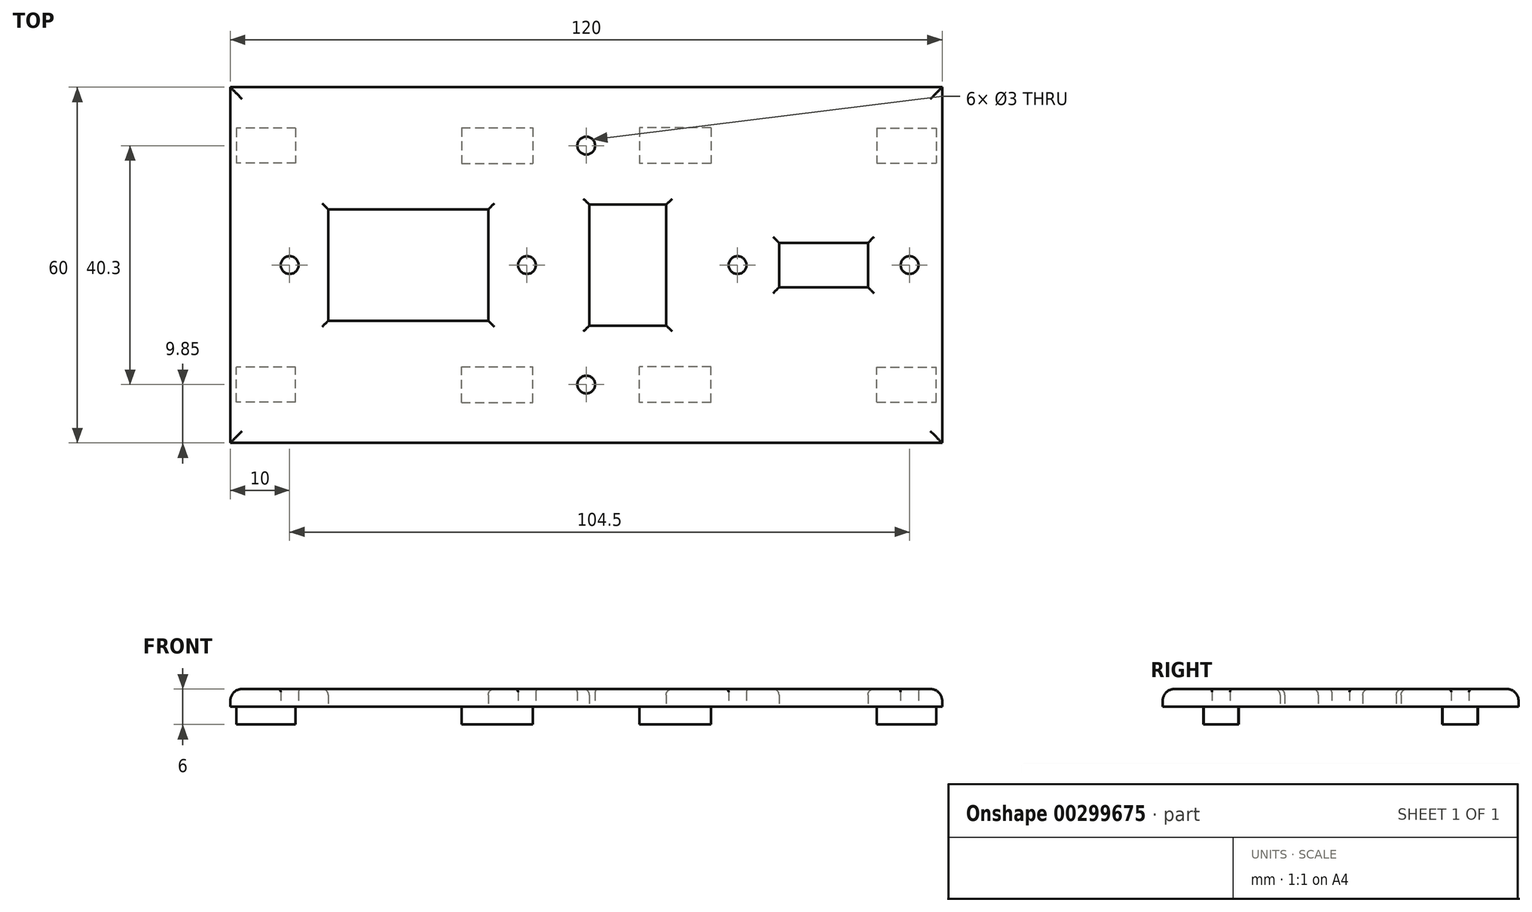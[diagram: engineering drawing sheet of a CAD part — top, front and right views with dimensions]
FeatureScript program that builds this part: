
annotation { "Feature Type Name" : "Feature", "Feature Type Description" : "" }
export const myFeature = defineFeature(function(context is Context, id is Id, definition is map)
    precondition{}
    {
        {
            var Q0;
            Q0=qCreatedBy(makeId("Top.planeOp"),FACE);
            var sketch = newSketch(context, id + "F0", { "sketchPlane" : qUnion([Q0])});
            skLineSegment(sketch, "E0.bottom", {"start": v(60, 30) * mm, "end": v(-60, 30) * mm});
            skLineSegment(sketch, "E0.top", {"start": v(60, -30) * mm, "end": v(-60, -30) * mm});
            skLineSegment(sketch, "E0.left", {"start": v(60, 30) * mm, "end": v(60, -30) * mm});
            skLineSegment(sketch, "E0.right", {"start": v(-60, 30) * mm, "end": v(-60, -30) * mm});
            skPoint(sketch, "E0.middle", {"position": v(0, 0) * mm});
            skLineSegment(sketch, "E1", {"start": v(0, 0) * mm, "end": v(0, 20.15) * mm, "construction": true});
            skLineSegment(sketch, "E2", {"start": v(-60, 20.15) * mm, "end": v(60, 20.15) * mm, "construction": true});
            skLineSegment(sketch, "E3", {"start": v(-60, 20.15) * mm, "end": v(-53.98, 20.15) * mm, "construction": true});
            skLineSegment(sketch, "E4.bottom", {"start": v(-48.98, 23.1) * mm, "end": v(-58.98, 23.1) * mm});
            skLineSegment(sketch, "E4.top", {"start": v(-48.98, 17.2) * mm, "end": v(-58.98, 17.2) * mm});
            skLineSegment(sketch, "E4.left", {"start": v(-48.98, 23.1) * mm, "end": v(-48.98, 17.2) * mm});
            skLineSegment(sketch, "E4.right", {"start": v(-58.98, 23.1) * mm, "end": v(-58.98, 17.2) * mm});
            skPoint(sketch, "E4.middle", {"position": v(-53.98, 20.15) * mm});
            skLineSegment(sketch, "E5", {"start": v(0, 20.15) * mm, "end": v(-15, 20.15) * mm, "construction": true});
            skLineSegment(sketch, "E6.bottom", {"start": v(-21.02, 23.15) * mm, "end": v(-8.98, 23.15) * mm});
            skLineSegment(sketch, "E6.top", {"start": v(-21.02, 17.15) * mm, "end": v(-8.98, 17.15) * mm});
            skLineSegment(sketch, "E6.left", {"start": v(-21.02, 23.15) * mm, "end": v(-21.02, 17.15) * mm});
            skLineSegment(sketch, "E6.right", {"start": v(-8.98, 23.15) * mm, "end": v(-8.98, 17.15) * mm});
            skPoint(sketch, "E6.middle", {"position": v(-15, 20.15) * mm});
            skLineSegment(sketch, "E7.MirrorCS", {"start": v(48.98, 23.1) * mm, "end": v(58.98, 23.1) * mm});
            skLineSegment(sketch, "E8.MirrorCS", {"start": v(48.98, 17.2) * mm, "end": v(58.98, 17.2) * mm});
            skLineSegment(sketch, "E9.MirrorCS", {"start": v(58.98, 23.1) * mm, "end": v(58.98, 17.2) * mm});
            skLineSegment(sketch, "E10.MirrorCS", {"start": v(48.98, 23.1) * mm, "end": v(48.98, 17.2) * mm});
            skLineSegment(sketch, "E11.MirrorCS", {"start": v(21.02, 17.15) * mm, "end": v(8.98, 17.15) * mm});
            skLineSegment(sketch, "E12.MirrorCS", {"start": v(21.02, 23.15) * mm, "end": v(8.98, 23.15) * mm});
            skLineSegment(sketch, "E13.MirrorCS", {"start": v(21.02, 23.15) * mm, "end": v(21.02, 17.15) * mm});
            skLineSegment(sketch, "E14.MirrorCS", {"start": v(8.98, 23.15) * mm, "end": v(8.98, 17.15) * mm});
            skLineSegment(sketch, "E15.MirrorCS", {"start": v(-58.98, -23.1) * mm, "end": v(-58.98, -17.2) * mm});
            skLineSegment(sketch, "E16.MirrorCS", {"start": v(-48.98, -23.1) * mm, "end": v(-48.98, -17.2) * mm});
            skLineSegment(sketch, "E17.MirrorCS", {"start": v(-21.02, -23.15) * mm, "end": v(-21.02, -17.15) * mm});
            skLineSegment(sketch, "E18.MirrorCS", {"start": v(-8.98, -23.15) * mm, "end": v(-8.98, -17.15) * mm});
            skLineSegment(sketch, "E19.MirrorCS", {"start": v(8.98, -23.15) * mm, "end": v(8.98, -17.15) * mm});
            skLineSegment(sketch, "E20.MirrorCS", {"start": v(21.02, -23.15) * mm, "end": v(21.02, -17.15) * mm});
            skLineSegment(sketch, "E21.MirrorCS", {"start": v(48.98, -23.1) * mm, "end": v(48.98, -17.2) * mm});
            skLineSegment(sketch, "E22.MirrorCS", {"start": v(58.98, -23.1) * mm, "end": v(58.98, -17.2) * mm});
            skLineSegment(sketch, "E23.MirrorCS", {"start": v(48.98, -23.1) * mm, "end": v(58.98, -23.1) * mm});
            skLineSegment(sketch, "E24.MirrorCS", {"start": v(21.02, -23.15) * mm, "end": v(8.98, -23.15) * mm});
            skLineSegment(sketch, "E25.MirrorCS", {"start": v(-21.02, -23.15) * mm, "end": v(-8.98, -23.15) * mm});
            skLineSegment(sketch, "E26.MirrorCS", {"start": v(-48.98, -23.1) * mm, "end": v(-58.98, -23.1) * mm});
            skLineSegment(sketch, "E27.MirrorCS", {"start": v(-48.98, -17.2) * mm, "end": v(-58.98, -17.2) * mm});
            skLineSegment(sketch, "E28.MirrorCS", {"start": v(-21.02, -17.15) * mm, "end": v(-8.98, -17.15) * mm});
            skLineSegment(sketch, "E29.MirrorCS", {"start": v(21.02, -17.15) * mm, "end": v(8.98, -17.15) * mm});
            skLineSegment(sketch, "E30.MirrorCS", {"start": v(48.98, -17.2) * mm, "end": v(58.98, -17.2) * mm});
            skLineSegment(sketch, "E31", {"start": v(0, 0) * mm, "end": v(-30, 0) * mm, "construction": true});
            skLineSegment(sketch, "E32.bottom", {"start": v(-43.5, -9.4) * mm, "end": v(-16.5, -9.4) * mm});
            skLineSegment(sketch, "E32.top", {"start": v(-43.5, 9.4) * mm, "end": v(-16.5, 9.4) * mm});
            skLineSegment(sketch, "E32.left", {"start": v(-43.5, -9.4) * mm, "end": v(-43.5, 9.4) * mm});
            skLineSegment(sketch, "E32.right", {"start": v(-16.5, -9.4) * mm, "end": v(-16.5, 9.4) * mm});
            skPoint(sketch, "E32.middle", {"position": v(-30, 0) * mm});
            skLineSegment(sketch, "E33", {"start": v(60, 0) * mm, "end": v(40, 0) * mm, "construction": true});
            skPoint(sketch, "E33.endSnap0", {"position": v(60, 0) * mm});
            skLineSegment(sketch, "E34.bottom", {"start": v(47.5, 3.75) * mm, "end": v(32.5, 3.75) * mm});
            skLineSegment(sketch, "E34.top", {"start": v(47.5, -3.75) * mm, "end": v(32.5, -3.75) * mm});
            skLineSegment(sketch, "E34.left", {"start": v(47.5, 3.75) * mm, "end": v(47.5, -3.75) * mm});
            skLineSegment(sketch, "E34.right", {"start": v(32.5, 3.75) * mm, "end": v(32.5, -3.75) * mm});
            skPoint(sketch, "E34.middle", {"position": v(40, 0) * mm});
            skLineSegment(sketch, "E35", {"start": v(-30, 0) * mm, "end": v(-50, 0) * mm, "construction": true});
            skLineSegment(sketch, "E36", {"start": v(-30, 0) * mm, "end": v(-10, 0) * mm, "construction": true});
            skCircle(sketch, "E37", {"center": v(-10, 0) * mm, "radius": 1.5 * mm});
            skLineSegment(sketch, "E38", {"start": v(-30, 0) * mm, "end": v(-30, 7) * mm, "construction": true});
            skCircle(sketch, "E39.MirrorC", {"center": v(-50, 0) * mm, "radius": 1.5 * mm});
            skLineSegment(sketch, "E40", {"start": v(40, 0) * mm, "end": v(25.5, 0) * mm, "construction": true});
            skLineSegment(sketch, "E41", {"start": v(40, 0) * mm, "end": v(40, 7) * mm, "construction": true});
            skPoint(sketch, "E41.endSnap0", {"position": v(40, 3.75) * mm});
            skCircle(sketch, "E42", {"center": v(25.5, 0) * mm, "radius": 1.5 * mm});
            skCircle(sketch, "E43.MirrorC", {"center": v(54.5, 0) * mm, "radius": 1.5 * mm});
            skCircle(sketch, "E44", {"center": v(0, 20.15) * mm, "radius": 1.5 * mm});
            skCircle(sketch, "E45.MirrorC", {"center": v(0, -20.15) * mm, "radius": 1.5 * mm});
            skLineSegment(sketch, "E46", {"start": v(0, 0) * mm, "end": v(7, 0) * mm, "construction": true});
            skLineSegment(sketch, "E47.bottom", {"start": v(13.47, 10.2) * mm, "end": v(0.52, 10.2) * mm});
            skLineSegment(sketch, "E47.top", {"start": v(13.48, -10.2) * mm, "end": v(0.53, -10.2) * mm});
            skLineSegment(sketch, "E47.left", {"start": v(13.47, 10.2) * mm, "end": v(13.48, -10.2) * mm});
            skLineSegment(sketch, "E47.right", {"start": v(0.52, 10.2) * mm, "end": v(0.53, -10.2) * mm});
            skPoint(sketch, "E47.middle", {"position": v(7, 0) * mm});
            skSolve(sketch);
        }
        {
            var Q0;
            Q0 = qSketchRegion(id + "F0", true);
            var Q1;
            Q1=makeQuery(id+"F0.imprint","IMPRINT",FACE,{"disambiguationData":[TD([[makeQuery(id+"F0.imprint","IMPRINT",EDGE,{"derivedFrom":sQuery(id+"F0.wireOp",EDGE,"E6.bottom")}),-1.0]])]});
            var Q2;
            Q2=makeQuery(id+"F0.imprint","IMPRINT",FACE,{"disambiguationData":[TD([[makeQuery(id+"F0.imprint","IMPRINT",EDGE,{"derivedFrom":sQuery(id+"F0.wireOp",EDGE,"E11.MirrorCS")}),-1.0]])]});
            var Q3;
            Q3=makeQuery(id+"F0.imprint","IMPRINT",FACE,{"disambiguationData":[TD([[makeQuery(id+"F0.imprint","IMPRINT",EDGE,{"derivedFrom":sQuery(id+"F0.wireOp",EDGE,"E19.MirrorCS")}),-1.0]])]});
            var Q4;
            Q4=makeQuery(id+"F0.imprint","IMPRINT",FACE,{"disambiguationData":[TD([[makeQuery(id+"F0.imprint","IMPRINT",EDGE,{"derivedFrom":sQuery(id+"F0.wireOp",EDGE,"E17.MirrorCS")}),-1.0]])]});
            var Q5;
            Q5=makeQuery(id+"F0.imprint","IMPRINT",FACE,{"disambiguationData":[TD([[makeQuery(id+"F0.imprint","IMPRINT",EDGE,{"derivedFrom":sQuery(id+"F0.wireOp",EDGE,"E4.bottom")}),1.0]])]});
            var Q6;
            Q6=makeQuery(id+"F0.imprint","IMPRINT",FACE,{"disambiguationData":[TD([[makeQuery(id+"F0.imprint","IMPRINT",EDGE,{"derivedFrom":sQuery(id+"F0.wireOp",EDGE,"E15.MirrorCS")}),-1.0]])]});
            var Q7;
            Q7=makeQuery(id+"F0.imprint","IMPRINT",FACE,{"disambiguationData":[TD([[makeQuery(id+"F0.imprint","IMPRINT",EDGE,{"derivedFrom":sQuery(id+"F0.wireOp",EDGE,"E21.MirrorCS")}),-1.0]])]});
            var Q8;
            Q8=makeQuery(id+"F0.imprint","IMPRINT",FACE,{"disambiguationData":[TD([[makeQuery(id+"F0.imprint","IMPRINT",EDGE,{"derivedFrom":sQuery(id+"F0.wireOp",EDGE,"E7.MirrorCS")}),-1.0]])]});
            extrude(context, id + "F1", {"entities" : qUnion([Q0, Q1, Q2, Q3, Q4, Q5, Q6, Q7, Q8]), "depth" : 3 * mm});
        }
        {
            var Q0;
            Q0=makeQuery(id+"F1.opExtrude","CAP_EDGE",EDGE,{"disambiguationData":[OSD([sQuery(id+"F0.wireOp",EDGE,"E0.top")])],"isStart":false});
            var Q1;
            Q1=makeQuery(id+"F1.opExtrude","CAP_EDGE",EDGE,{"disambiguationData":[OSD([sQuery(id+"F0.wireOp",EDGE,"E0.bottom")])],"isStart":false});
            var Q2;
            Q2=makeQuery(id+"F1.opExtrude","CAP_EDGE",EDGE,{"disambiguationData":[OSD([sQuery(id+"F0.wireOp",EDGE,"E0.right")])],"isStart":false});
            var Q3;
            Q3=makeQuery(id+"F1.opExtrude","CAP_EDGE",EDGE,{"disambiguationData":[OSD([sQuery(id+"F0.wireOp",EDGE,"E0.left")])],"isStart":false});
            fillet(context, id + "F2", {"entities" : qUnion([Q0, Q1, Q2, Q3]), "radius" : 2 * mm, "tangentPropagation" : true, "allowEdgeOverflow" : false});
        }
        {
            var Q0;
            Q0=makeQuery(id+"F1.opExtrude","CAP_EDGE",EDGE,{"disambiguationData":[OSD([sQuery(id+"F0.wireOp",EDGE,"E34.left")])],"isStart":false});
            var Q1;
            Q1=makeQuery(id+"F1.opExtrude","CAP_EDGE",EDGE,{"disambiguationData":[OSD([sQuery(id+"F0.wireOp",EDGE,"E34.right")])],"isStart":false});
            var Q2;
            Q2=makeQuery(id+"F1.opExtrude","CAP_EDGE",EDGE,{"disambiguationData":[OSD([sQuery(id+"F0.wireOp",EDGE,"E34.bottom")])],"isStart":false});
            var Q3;
            Q3=makeQuery(id+"F1.opExtrude","CAP_EDGE",EDGE,{"disambiguationData":[OSD([sQuery(id+"F0.wireOp",EDGE,"E34.top")])],"isStart":false});
            var Q4;
            Q4=makeQuery(id+"F1.opExtrude","CAP_EDGE",EDGE,{"disambiguationData":[OSD([sQuery(id+"F0.wireOp",EDGE,"E32.top")])],"isStart":false});
            var Q5;
            Q5=makeQuery(id+"F1.opExtrude","CAP_EDGE",EDGE,{"disambiguationData":[OSD([sQuery(id+"F0.wireOp",EDGE,"E32.bottom")])],"isStart":false});
            var Q6;
            Q6=makeQuery(id+"F1.opExtrude","CAP_EDGE",EDGE,{"disambiguationData":[OSD([sQuery(id+"F0.wireOp",EDGE,"E32.left")])],"isStart":false});
            var Q7;
            Q7=makeQuery(id+"F1.opExtrude","CAP_EDGE",EDGE,{"disambiguationData":[OSD([sQuery(id+"F0.wireOp",EDGE,"E32.right")])],"isStart":false});
            var Q8;
            Q8=makeQuery(id+"F1.opExtrude","CAP_EDGE",EDGE,{"disambiguationData":[OSD([sQuery(id+"F0.wireOp",EDGE,"E47.left")])],"isStart":false});
            var Q9;
            Q9=makeQuery(id+"F1.opExtrude","CAP_EDGE",EDGE,{"disambiguationData":[OSD([sQuery(id+"F0.wireOp",EDGE,"E47.right")])],"isStart":false});
            var Q10;
            Q10=makeQuery(id+"F1.opExtrude","CAP_EDGE",EDGE,{"disambiguationData":[OSD([sQuery(id+"F0.wireOp",EDGE,"E47.bottom")])],"isStart":false});
            var Q11;
            Q11=makeQuery(id+"F1.opExtrude","CAP_EDGE",EDGE,{"disambiguationData":[OSD([sQuery(id+"F0.wireOp",EDGE,"E47.top")])],"isStart":false});
            fillet(context, id + "F3", {"entities" : qUnion([Q0, Q1, Q2, Q3, Q4, Q5, Q6, Q7, Q8, Q9, Q10, Q11]), "radius" : 1 * mm, "tangentPropagation" : true, "allowEdgeOverflow" : false});
        }
        {
            var Q0;
            Q0=makeQuery(id+"F1.opExtrude","CAP_EDGE",EDGE,{"disambiguationData":[OSD([sQuery(id+"F0.wireOp",EDGE,"E39.MirrorC")])],"isStart":false});
            var Q1;
            Q1=makeQuery(id+"F1.opExtrude","CAP_EDGE",EDGE,{"disambiguationData":[OSD([sQuery(id+"F0.wireOp",EDGE,"E37")])],"isStart":false});
            var Q2;
            Q2=makeQuery(id+"F1.opExtrude","CAP_EDGE",EDGE,{"disambiguationData":[OSD([sQuery(id+"F0.wireOp",EDGE,"E42")])],"isStart":false});
            var Q3;
            Q3=makeQuery(id+"F1.opExtrude","CAP_EDGE",EDGE,{"disambiguationData":[OSD([sQuery(id+"F0.wireOp",EDGE,"E43.MirrorC")])],"isStart":false});
            var Q4;
            Q4=makeQuery(id+"F1.opExtrude","CAP_EDGE",EDGE,{"disambiguationData":[OSD([sQuery(id+"F0.wireOp",EDGE,"E45.MirrorC")])],"isStart":false});
            var Q5;
            Q5=makeQuery(id+"F1.opExtrude","CAP_EDGE",EDGE,{"disambiguationData":[OSD([sQuery(id+"F0.wireOp",EDGE,"E44")])],"isStart":false});
            fillet(context, id + "F4", {"entities" : qUnion([Q0, Q1, Q2, Q3, Q4, Q5]), "radius" : 0.5 * mm, "tangentPropagation" : true, "allowEdgeOverflow" : false});
        }
        {
            var Q0;
            Q0=makeQuery(id+"F0.imprint","IMPRINT",FACE,{"disambiguationData":[TD([[makeQuery(id+"F0.imprint","IMPRINT",EDGE,{"derivedFrom":sQuery(id+"F0.wireOp",EDGE,"E7.MirrorCS")}),-1.0]])]});
            var Q1;
            Q1=makeQuery(id+"F0.imprint","IMPRINT",FACE,{"disambiguationData":[TD([[makeQuery(id+"F0.imprint","IMPRINT",EDGE,{"derivedFrom":sQuery(id+"F0.wireOp",EDGE,"E11.MirrorCS")}),-1.0]])]});
            var Q2;
            Q2=makeQuery(id+"F0.imprint","IMPRINT",FACE,{"disambiguationData":[TD([[makeQuery(id+"F0.imprint","IMPRINT",EDGE,{"derivedFrom":sQuery(id+"F0.wireOp",EDGE,"E6.bottom")}),-1.0]])]});
            var Q3;
            Q3=makeQuery(id+"F0.imprint","IMPRINT",FACE,{"disambiguationData":[TD([[makeQuery(id+"F0.imprint","IMPRINT",EDGE,{"derivedFrom":sQuery(id+"F0.wireOp",EDGE,"E4.bottom")}),1.0]])]});
            var Q4;
            Q4=makeQuery(id+"F0.imprint","IMPRINT",FACE,{"disambiguationData":[TD([[makeQuery(id+"F0.imprint","IMPRINT",EDGE,{"derivedFrom":sQuery(id+"F0.wireOp",EDGE,"E15.MirrorCS")}),-1.0]])]});
            var Q5;
            Q5=makeQuery(id+"F0.imprint","IMPRINT",FACE,{"disambiguationData":[TD([[makeQuery(id+"F0.imprint","IMPRINT",EDGE,{"derivedFrom":sQuery(id+"F0.wireOp",EDGE,"E17.MirrorCS")}),-1.0]])]});
            var Q6;
            Q6=makeQuery(id+"F0.imprint","IMPRINT",FACE,{"disambiguationData":[TD([[makeQuery(id+"F0.imprint","IMPRINT",EDGE,{"derivedFrom":sQuery(id+"F0.wireOp",EDGE,"E19.MirrorCS")}),-1.0]])]});
            var Q7;
            Q7=makeQuery(id+"F0.imprint","IMPRINT",FACE,{"disambiguationData":[TD([[makeQuery(id+"F0.imprint","IMPRINT",EDGE,{"derivedFrom":sQuery(id+"F0.wireOp",EDGE,"E21.MirrorCS")}),-1.0]])]});
            extrude(context, id + "F5", {"entities" : qUnion([Q0, Q1, Q2, Q3, Q4, Q5, Q6, Q7]), "operationType" : NewBodyOperationType.ADD, "oppositeDirection" : true, "depth" : 3 * mm});
        }
    });
